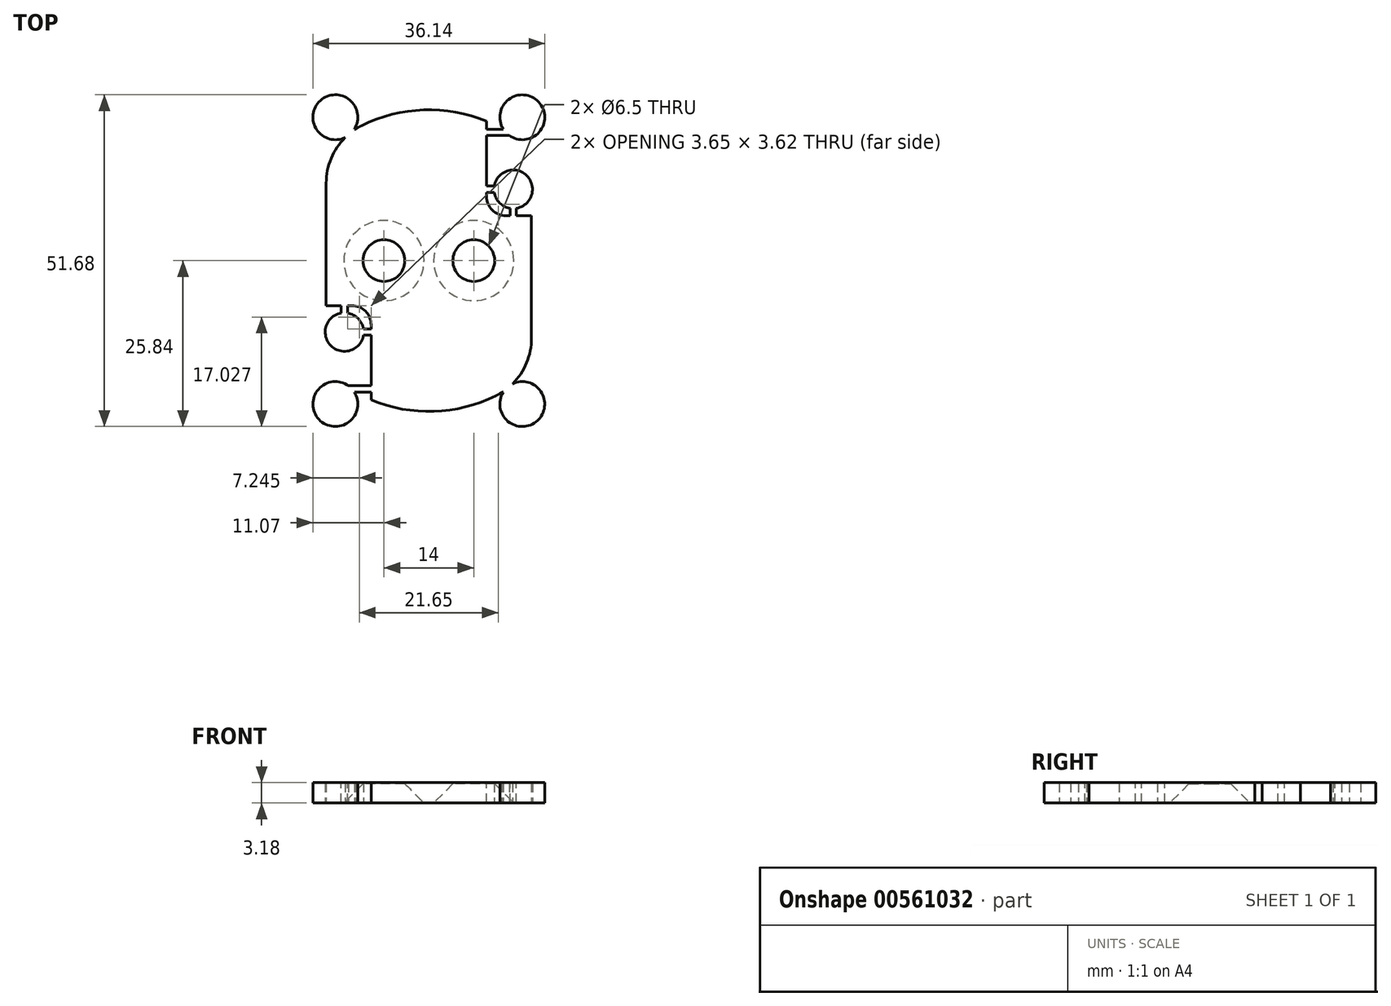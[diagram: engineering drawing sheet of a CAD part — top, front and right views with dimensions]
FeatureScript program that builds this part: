
annotation { "Feature Type Name" : "Feature", "Feature Type Description" : "" }
export const myFeature = defineFeature(function(context is Context, id is Id, definition is map)
    precondition{}
    {
        {
            var Q0;
            Q0=qCreatedBy(makeId("Top.planeOp"),FACE);
            var sketch = newSketch(context, id + "F0", { "sketchPlane" : qUnion([Q0])});
            skArc(sketch, "E0", {"start": v(9, 21.7) * mm, "mid": v(-0.8, 23.49) * mm, "end": v(-10.44, 21.05) * mm});
            skLineSegment(sketch, "E1", {"start": v(9, 21.7) * mm, "end": v(9, 10) * mm});
            skLineSegment(sketch, "E2", {"start": v(12, 7) * mm, "end": v(16, 7) * mm});
            skLineSegment(sketch, "E3", {"start": v(-9, -21.7) * mm, "end": v(-9, -10) * mm});
            skLineSegment(sketch, "E4", {"start": v(-12, -7) * mm, "end": v(-16, -7) * mm});
            skArc(sketch, "E5.trimOffspring", {"start": v(-9, -21.7) * mm, "mid": v(0.8, -23.49) * mm, "end": v(10.44, -21.05) * mm});
            skLineSegment(sketch, "E6", {"start": v(-16, -7) * mm, "end": v(-16, 12.1) * mm});
            skLineSegment(sketch, "E7", {"start": v(16, 7) * mm, "end": v(16, -12.1) * mm});
            skPoint(sketch, "E8.visualSharp", {"position": v(9, 7) * mm});
            skArc(sketch, "E8.filletArc", {"start": v(9, 10) * mm, "mid": v(9.88, 7.88) * mm, "end": v(12, 7) * mm});
            skPoint(sketch, "E9.visualSharp", {"position": v(-9, -7) * mm});
            skArc(sketch, "E9.filletArc", {"start": v(-9, -10) * mm, "mid": v(-9.88, -7.88) * mm, "end": v(-12, -7) * mm});
            skPoint(sketch, "E10.visualSharp", {"position": v(16, -17.21) * mm});
            skArc(sketch, "E10.filletArc", {"start": v(10.44, -21.05) * mm, "mid": v(14.5, -17.36) * mm, "end": v(16, -12.1) * mm});
            skPoint(sketch, "E11.visualSharp", {"position": v(-16, 17.21) * mm});
            skArc(sketch, "E11.filletArc", {"start": v(-10.44, 21.05) * mm, "mid": v(-14.5, 17.36) * mm, "end": v(-16, 12.1) * mm});
            skCircle(sketch, "E12", {"center": v(-25, -13.13) * mm, "radius": 2.75 * mm, "construction": true});
            skCircle(sketch, "E13.0", {"center": v(-25, -13.13) * mm, "radius": 3.75 * mm, "construction": true});
            skLineSegment(sketch, "E14", {"start": v(-16, 0) * mm, "end": v(16, 0) * mm, "construction": true});
            skLineSegment(sketch, "E15", {"start": v(0, 23.5) * mm, "end": v(0, -23.5) * mm, "construction": true});
            skCircle(sketch, "E16", {"center": v(-7, 0) * mm, "radius": 3.25 * mm});
            skCircle(sketch, "E17", {"center": v(7, 0) * mm, "radius": 3.25 * mm});
            skSolve(sketch);
        }
        {
            var Q0;
            Q0 = qSketchRegion(id + "F0", true);
            extrude(context, id + "F1", {"entities" : qUnion([Q0]), "depth" : 3.17 * mm, "offsetDistance" : 25 * mm});
        }
        {
            var Q0;
            Q0=makeQuery(id+"F1.opExtrude","CAP_EDGE",EDGE,{"disambiguationData":[OSD([sQuery(id+"F0.wireOp",EDGE,"E16")])],"isStart":true});
            var Q1;
            Q1=makeQuery(id+"F1.opExtrude","CAP_EDGE",EDGE,{"disambiguationData":[OSD([sQuery(id+"F0.wireOp",EDGE,"E17")])],"isStart":true});
            chamfer(context, id + "F2", {"entities" : qUnion([Q0, Q1]), "width" : 3 * mm, "tangentPropagation" : true});
        }
        {
            var Q0;
            {var subQ0=sQuery(id+"F0.wireOp",EDGE,"E11.filletArc");var subQ1=sQuery(id+"F0.wireOp",EDGE,"E10.filletArc");var subQ2=sQuery(id+"F0.wireOp",EDGE,"E9.filletArc");var subQ3=sQuery(id+"F0.wireOp",EDGE,"E2");var subQ4=sQuery(id+"F0.wireOp",EDGE,"E1");var subQ5=sQuery(id+"F0.wireOp",EDGE,"E17");var subQ6=sQuery(id+"F0.wireOp",EDGE,"E16");var subQ7=sQuery(id+"F0.wireOp",EDGE,"E8.filletArc");var subQ8=sQuery(id+"F0.wireOp",EDGE,"E7");var subQ9=sQuery(id+"F0.wireOp",EDGE,"E6");var subQ10=sQuery(id+"F0.wireOp",EDGE,"E5.trimOffspring");var subQ11=sQuery(id+"F0.wireOp",EDGE,"E4");var subQ12=sQuery(id+"F0.wireOp",EDGE,"E3");var subQ13=sQuery(id+"F0.wireOp",EDGE,"E0");var subQ14=makeQuery(id+"F1.opExtrude","CAP_FACE",FACE,{"disambiguationData":[OSD([subQ13,subQ4,subQ3,subQ12,subQ11,subQ10,subQ9,subQ8,subQ7,subQ2,subQ1,subQ0,subQ6,subQ5])],"isStart":true});Q0=makeQuery(id+"F7rJXuFzd7whJRI_1.boolean.opBoolean","SPLIT",FACE,{"disambiguationData":[TD([makeQuery(id+"F1.opExtrude","SWEPT_FACE",FACE,{"disambiguationData":[OSD([subQ13])]}),subQ14,makeQuery(id+"F1.opExtrude","SWEPT_FACE",FACE,{"disambiguationData":[OSD([subQ4])]}),makeQuery(id+"F1.opExtrude","SWEPT_FACE",FACE,{"disambiguationData":[OSD([subQ3])]}),makeQuery(id+"F1.opExtrude","SWEPT_FACE",FACE,{"disambiguationData":[OSD([subQ12])]}),makeQuery(id+"F1.opExtrude","SWEPT_FACE",FACE,{"disambiguationData":[OSD([subQ11])]}),makeQuery(id+"F1.opExtrude","SWEPT_FACE",FACE,{"disambiguationData":[OSD([subQ10])]}),makeQuery(id+"F1.opExtrude","SWEPT_FACE",FACE,{"disambiguationData":[OSD([subQ9])]}),makeQuery(id+"F1.opExtrude","SWEPT_FACE",FACE,{"disambiguationData":[OSD([subQ8])]}),makeQuery(id+"F1.opExtrude","SWEPT_FACE",FACE,{"disambiguationData":[OSD([subQ7])]}),makeQuery(id+"F1.opExtrude","SWEPT_FACE",FACE,{"disambiguationData":[OSD([subQ2])]}),makeQuery(id+"F1.opExtrude","SWEPT_FACE",FACE,{"disambiguationData":[OSD([subQ1])]}),makeQuery(id+"F1.opExtrude","SWEPT_FACE",FACE,{"disambiguationData":[OSD([subQ0])]}),makeQuery(id+"F2.opChamfer","BLEND_FACE",FACE,{"disambiguationData":[OSD([subQ6])]}),makeQuery(id+"F2.opChamfer","BLEND_FACE",FACE,{"disambiguationData":[OSD([subQ5])]}),makeQuery(id+"FJRN7x09wjddpbt_1.opExtrude","SWEPT_FACE",FACE,{"disambiguationData":[OSD([sQuery(id+"F7eSavBRXq2dsKI_1.wireOp",EDGE,"8fa0daad-dcc6-40bc-96bb-e75cae0788b3.0"),sQuery(id+"F7eSavBRXq2dsKI_1.wireOp",EDGE,"n97fCblB-dYT1-Ae0N-i9l5-hArpFE4WxoEw"),sQuery(id+"F7eSavBRXq2dsKI_1.wireOp",EDGE,"zqmUF0HG-ZMKi-8qrd-Ef0Q-vBSs0Mmfe9LQ")])]}),makeQuery(id+"FJRN7x09wjddpbt_1.opExtrude","SWEPT_FACE",FACE,{"disambiguationData":[OSD([sQuery(id+"F7eSavBRXq2dsKI_1.wireOp",EDGE,"e7dde7e7-45df-4180-b28b-b804ea4044e9.0"),sQuery(id+"F7eSavBRXq2dsKI_1.wireOp",EDGE,"sIQKzWda-6bcH-76ju-v0o7-Y5VWPazvYRRh")])]}),makeQuery(id+"FJRN7x09wjddpbt_1.opExtrude","SWEPT_FACE",FACE,{"disambiguationData":[OSD([sQuery(id+"F7eSavBRXq2dsKI_1.wireOp",EDGE,"e2ec28e7-3c61-4beb-a361-8ff4288dedb5.0"),sQuery(id+"F7eSavBRXq2dsKI_1.wireOp",EDGE,"FANFZC1z-x6Kr-yiFN-UvMI-yiw826xu6Ap1"),sQuery(id+"F7eSavBRXq2dsKI_1.wireOp",EDGE,"g5gt4XFT-gkoA-6hYA-Hcyk-9ZKPAERTy8uj")])]}),makeQuery(id+"FJRN7x09wjddpbt_1.opExtrude","SWEPT_FACE",FACE,{"disambiguationData":[OSD([sQuery(id+"F7eSavBRXq2dsKI_1.wireOp",EDGE,"114f5c74-5dc2-4418-9fc7-5e99572f52d0.0"),sQuery(id+"F7eSavBRXq2dsKI_1.wireOp",EDGE,"zSLGWUzL-SdZn-Svw3-gUv4-kZl9FifSsFUy")])]}),makeQuery(id+"FJRN7x09wjddpbt_1.opExtrude","SWEPT_FACE",FACE,{"disambiguationData":[OSD([sQuery(id+"F7eSavBRXq2dsKI_1.wireOp",EDGE,"nJadRcHw-teo3-5osU-S39U-DkAnWl3BXwkZ")])]}),makeQuery(id+"FJRN7x09wjddpbt_1.opExtrude","SWEPT_FACE",FACE,{"disambiguationData":[OSD([sQuery(id+"F7eSavBRXq2dsKI_1.wireOp",EDGE,"ttBzBW3A-ctuH-0JyX-jzIS-FURpFCNeuO8h")])]}),makeQuery(id+"F7rJXuFzd7whJRI_1.opExtrude","SWEPT_FACE",FACE,{"disambiguationData":[OSD([sQuery(id+"FJmdBiUrNK7vk2C_1.wireOp",EDGE,"6ccd15b6-2c7d-49c7-b1f2-da74a62637db.0")])]}),makeQuery(id+"F7rJXuFzd7whJRI_1.opExtrude","SWEPT_FACE",FACE,{"disambiguationData":[OSD([sQuery(id+"FJmdBiUrNK7vk2C_1.wireOp",EDGE,"40ce07cb-99c2-479f-b22f-8af0174601d0.0")])]}),makeQuery(id+"F7rJXuFzd7whJRI_1.opExtrude","SWEPT_FACE",FACE,{"disambiguationData":[OSD([sQuery(id+"FJmdBiUrNK7vk2C_1.wireOp",EDGE,"78c2ad54-c2ae-4de3-8f60-8a07646ae407.0")])]}),makeQuery(id+"F7rJXuFzd7whJRI_1.opExtrude","SWEPT_FACE",FACE,{"disambiguationData":[OSD([sQuery(id+"FJmdBiUrNK7vk2C_1.wireOp",EDGE,"a5992d94-6c83-43fa-9fcd-ea2cdb8489dd.0")])]}),makeQuery(id+"F7rJXuFzd7whJRI_1.opExtrude","SWEPT_FACE",FACE,{"disambiguationData":[OSD([sQuery(id+"FJmdBiUrNK7vk2C_1.wireOp",EDGE,"94c68105-d2c2-4680-80d6-486de9ed9849.0")])]}),makeQuery(id+"F7rJXuFzd7whJRI_1.opExtrude","SWEPT_FACE",FACE,{"disambiguationData":[OSD([sQuery(id+"FJmdBiUrNK7vk2C_1.wireOp",EDGE,"5a1a2a42-ccab-4370-b0ba-2aafa13ec267.0")])]}),makeQuery(id+"F7rJXuFzd7whJRI_1.opExtrude","SWEPT_FACE",FACE,{"disambiguationData":[OSD([sQuery(id+"FJmdBiUrNK7vk2C_1.wireOp",EDGE,"b4e74ed3-bff9-4cb2-9b7f-92468b897526.0")])]}),makeQuery(id+"F7rJXuFzd7whJRI_1.opExtrude","SWEPT_FACE",FACE,{"disambiguationData":[OSD([sQuery(id+"FJmdBiUrNK7vk2C_1.wireOp",EDGE,"bb4724f0-601e-4360-ab2a-57e4bcc06b99.0")])]}),makeQuery(id+"F7rJXuFzd7whJRI_1.opExtrude","SWEPT_FACE",FACE,{"disambiguationData":[OSD([sQuery(id+"FJmdBiUrNK7vk2C_1.wireOp",EDGE,"uudjV1i5-Grv9-P5jP-yEU4-0d5r7IUhJ2e0")])]}),makeQuery(id+"F7rJXuFzd7whJRI_1.opExtrude","SWEPT_FACE",FACE,{"disambiguationData":[OSD([sQuery(id+"FJmdBiUrNK7vk2C_1.wireOp",EDGE,"BnZCvLlh-3Oxl-QPef-bhhu-gMUTPy8vweJf")])]}),makeQuery(id+"F7rJXuFzd7whJRI_1.opExtrude","SWEPT_FACE",FACE,{"disambiguationData":[OSD([sQuery(id+"FJmdBiUrNK7vk2C_1.wireOp",EDGE,"tRLUp6J2-3hZ5-DYTa-A9Ly-egRAl724t58r")])]}),makeQuery(id+"F7rJXuFzd7whJRI_1.opExtrude","SWEPT_FACE",FACE,{"disambiguationData":[OSD([sQuery(id+"FJmdBiUrNK7vk2C_1.wireOp",EDGE,"19JWv38y-xvaW-ymGE-MEyl-ytO9JCIOFrmj")])]})])],"derivedFrom":subQ14});}
            var sketch = newSketch(context, id + "F3", { "sketchPlane" : qUnion([Q0])});
            skCircle(sketch, "E18", {"center": v(-13.15, 11.12) * mm, "radius": 3 * mm});
            skLineSegment(sketch, "E19", {"start": v(-7, 0) * mm, "end": v(7, 0) * mm, "construction": true});
            skLineSegment(sketch, "E20", {"start": v(0, 7) * mm, "end": v(0, -7) * mm, "construction": true});
            skCircle(sketch, "E21.MirrorC", {"center": v(13.15, -11.12) * mm, "radius": 3 * mm});
            skLineSegment(sketch, "E22.bottom", {"start": v(-6, 11.62) * mm, "end": v(-12, 11.62) * mm});
            skLineSegment(sketch, "E22.top", {"start": v(-6, 10.62) * mm, "end": v(-12, 10.62) * mm});
            skLineSegment(sketch, "E22.left", {"start": v(-6, 11.62) * mm, "end": v(-6, 10.62) * mm});
            skLineSegment(sketch, "E22.right", {"start": v(-12, 11.62) * mm, "end": v(-12, 10.62) * mm});
            skPoint(sketch, "E22.middle", {"position": v(-9, 11.12) * mm});
            skLineSegment(sketch, "E23.bottom", {"start": v(-12.65, 4) * mm, "end": v(-13.65, 4) * mm});
            skLineSegment(sketch, "E23.top", {"start": v(-12.65, 10) * mm, "end": v(-13.65, 10) * mm});
            skLineSegment(sketch, "E23.left", {"start": v(-12.65, 4) * mm, "end": v(-12.65, 10) * mm});
            skLineSegment(sketch, "E23.right", {"start": v(-13.65, 4) * mm, "end": v(-13.65, 10) * mm});
            skPoint(sketch, "E23.middle", {"position": v(-13.15, 7) * mm});
            skLineSegment(sketch, "E24.bottom", {"start": v(13.65, -4) * mm, "end": v(12.65, -4) * mm});
            skLineSegment(sketch, "E24.top", {"start": v(13.65, -10) * mm, "end": v(12.65, -10) * mm});
            skLineSegment(sketch, "E24.left", {"start": v(13.65, -4) * mm, "end": v(13.65, -10) * mm});
            skLineSegment(sketch, "E24.right", {"start": v(12.65, -4) * mm, "end": v(12.65, -10) * mm});
            skPoint(sketch, "E24.middle", {"position": v(13.15, -7) * mm});
            skLineSegment(sketch, "E25.bottom", {"start": v(6, -11.62) * mm, "end": v(12, -11.62) * mm});
            skLineSegment(sketch, "E25.top", {"start": v(6, -10.62) * mm, "end": v(12, -10.62) * mm});
            skLineSegment(sketch, "E25.left", {"start": v(6, -11.62) * mm, "end": v(6, -10.62) * mm});
            skLineSegment(sketch, "E25.right", {"start": v(12, -11.62) * mm, "end": v(12, -10.62) * mm});
            skPoint(sketch, "E25.middle", {"position": v(9, -11.12) * mm});
            skSolve(sketch);
        }
        {
            var Q0;
            Q0 = qSketchRegion(id + "F3", true);
            var Q1;
            Q1=makeQuery(id+"F1.opExtrude","CAP_FACE",FACE,{"disambiguationData":[OSD([sQuery(id+"F0.wireOp",EDGE,"E0"),sQuery(id+"F0.wireOp",EDGE,"E1"),sQuery(id+"F0.wireOp",EDGE,"E2"),sQuery(id+"F0.wireOp",EDGE,"E3"),sQuery(id+"F0.wireOp",EDGE,"E4"),sQuery(id+"F0.wireOp",EDGE,"E5.trimOffspring"),sQuery(id+"F0.wireOp",EDGE,"E6"),sQuery(id+"F0.wireOp",EDGE,"E7"),sQuery(id+"F0.wireOp",EDGE,"E8.filletArc"),sQuery(id+"F0.wireOp",EDGE,"E9.filletArc"),sQuery(id+"F0.wireOp",EDGE,"E10.filletArc"),sQuery(id+"F0.wireOp",EDGE,"E11.filletArc"),sQuery(id+"F0.wireOp",EDGE,"E16"),sQuery(id+"F0.wireOp",EDGE,"E17")])],"isStart":false});
            extrude(context, id + "F4", {"entities" : qUnion([Q0]), "operationType" : NewBodyOperationType.ADD, "endBound" : BoundingType.UP_TO_SURFACE, "oppositeDirection" : true, "depth" : 25 * mm, "endBoundEntityFace" : qUnion([Q1]), "offsetDistance" : 25 * mm});
        }
        {
            var Q0;
            {var subQ0=sQuery(id+"F0.wireOp",EDGE,"E11.filletArc");var subQ1=sQuery(id+"F0.wireOp",EDGE,"E10.filletArc");var subQ2=sQuery(id+"F0.wireOp",EDGE,"E9.filletArc");var subQ3=sQuery(id+"F0.wireOp",EDGE,"E2");var subQ4=sQuery(id+"F0.wireOp",EDGE,"E1");var subQ5=sQuery(id+"F0.wireOp",EDGE,"E17");var subQ6=sQuery(id+"F0.wireOp",EDGE,"E16");var subQ7=sQuery(id+"F0.wireOp",EDGE,"E8.filletArc");var subQ8=sQuery(id+"F0.wireOp",EDGE,"E7");var subQ9=sQuery(id+"F0.wireOp",EDGE,"E6");var subQ10=sQuery(id+"F0.wireOp",EDGE,"E5.trimOffspring");var subQ11=sQuery(id+"F0.wireOp",EDGE,"E4");var subQ12=sQuery(id+"F0.wireOp",EDGE,"E3");var subQ13=sQuery(id+"F0.wireOp",EDGE,"E0");var subQ14=makeQuery(id+"F1.opExtrude","CAP_FACE",FACE,{"disambiguationData":[OSD([subQ13,subQ4,subQ3,subQ12,subQ11,subQ10,subQ9,subQ8,subQ7,subQ2,subQ1,subQ0,subQ6,subQ5])],"isStart":true});Q0=makeQuery(id+"F4.boolean.opBoolean","MERGE",FACE,{"derivedFrom":[makeQuery(id+"F7rJXuFzd7whJRI_1.boolean.opBoolean","SPLIT",FACE,{"disambiguationData":[TD([makeQuery(id+"F1.opExtrude","SWEPT_FACE",FACE,{"disambiguationData":[OSD([subQ13])]}),subQ14,makeQuery(id+"F1.opExtrude","SWEPT_FACE",FACE,{"disambiguationData":[OSD([subQ4])]}),makeQuery(id+"F1.opExtrude","SWEPT_FACE",FACE,{"disambiguationData":[OSD([subQ3])]}),makeQuery(id+"F1.opExtrude","SWEPT_FACE",FACE,{"disambiguationData":[OSD([subQ12])]}),makeQuery(id+"F1.opExtrude","SWEPT_FACE",FACE,{"disambiguationData":[OSD([subQ11])]}),makeQuery(id+"F1.opExtrude","SWEPT_FACE",FACE,{"disambiguationData":[OSD([subQ10])]}),makeQuery(id+"F1.opExtrude","SWEPT_FACE",FACE,{"disambiguationData":[OSD([subQ9])]}),makeQuery(id+"F1.opExtrude","SWEPT_FACE",FACE,{"disambiguationData":[OSD([subQ8])]}),makeQuery(id+"F1.opExtrude","SWEPT_FACE",FACE,{"disambiguationData":[OSD([subQ7])]}),makeQuery(id+"F1.opExtrude","SWEPT_FACE",FACE,{"disambiguationData":[OSD([subQ2])]}),makeQuery(id+"F1.opExtrude","SWEPT_FACE",FACE,{"disambiguationData":[OSD([subQ1])]}),makeQuery(id+"F1.opExtrude","SWEPT_FACE",FACE,{"disambiguationData":[OSD([subQ0])]}),makeQuery(id+"F2.opChamfer","BLEND_FACE",FACE,{"disambiguationData":[OSD([subQ6])]}),makeQuery(id+"F2.opChamfer","BLEND_FACE",FACE,{"disambiguationData":[OSD([subQ5])]}),makeQuery(id+"FJRN7x09wjddpbt_1.opExtrude","SWEPT_FACE",FACE,{"disambiguationData":[OSD([sQuery(id+"F7eSavBRXq2dsKI_1.wireOp",EDGE,"8fa0daad-dcc6-40bc-96bb-e75cae0788b3.0"),sQuery(id+"F7eSavBRXq2dsKI_1.wireOp",EDGE,"n97fCblB-dYT1-Ae0N-i9l5-hArpFE4WxoEw"),sQuery(id+"F7eSavBRXq2dsKI_1.wireOp",EDGE,"zqmUF0HG-ZMKi-8qrd-Ef0Q-vBSs0Mmfe9LQ")])]}),makeQuery(id+"FJRN7x09wjddpbt_1.opExtrude","SWEPT_FACE",FACE,{"disambiguationData":[OSD([sQuery(id+"F7eSavBRXq2dsKI_1.wireOp",EDGE,"e7dde7e7-45df-4180-b28b-b804ea4044e9.0"),sQuery(id+"F7eSavBRXq2dsKI_1.wireOp",EDGE,"sIQKzWda-6bcH-76ju-v0o7-Y5VWPazvYRRh")])]}),makeQuery(id+"FJRN7x09wjddpbt_1.opExtrude","SWEPT_FACE",FACE,{"disambiguationData":[OSD([sQuery(id+"F7eSavBRXq2dsKI_1.wireOp",EDGE,"e2ec28e7-3c61-4beb-a361-8ff4288dedb5.0"),sQuery(id+"F7eSavBRXq2dsKI_1.wireOp",EDGE,"FANFZC1z-x6Kr-yiFN-UvMI-yiw826xu6Ap1"),sQuery(id+"F7eSavBRXq2dsKI_1.wireOp",EDGE,"g5gt4XFT-gkoA-6hYA-Hcyk-9ZKPAERTy8uj")])]}),makeQuery(id+"FJRN7x09wjddpbt_1.opExtrude","SWEPT_FACE",FACE,{"disambiguationData":[OSD([sQuery(id+"F7eSavBRXq2dsKI_1.wireOp",EDGE,"114f5c74-5dc2-4418-9fc7-5e99572f52d0.0"),sQuery(id+"F7eSavBRXq2dsKI_1.wireOp",EDGE,"zSLGWUzL-SdZn-Svw3-gUv4-kZl9FifSsFUy")])]}),makeQuery(id+"FJRN7x09wjddpbt_1.opExtrude","SWEPT_FACE",FACE,{"disambiguationData":[OSD([sQuery(id+"F7eSavBRXq2dsKI_1.wireOp",EDGE,"nJadRcHw-teo3-5osU-S39U-DkAnWl3BXwkZ")])]}),makeQuery(id+"FJRN7x09wjddpbt_1.opExtrude","SWEPT_FACE",FACE,{"disambiguationData":[OSD([sQuery(id+"F7eSavBRXq2dsKI_1.wireOp",EDGE,"ttBzBW3A-ctuH-0JyX-jzIS-FURpFCNeuO8h")])]}),makeQuery(id+"F7rJXuFzd7whJRI_1.opExtrude","SWEPT_FACE",FACE,{"disambiguationData":[OSD([sQuery(id+"FJmdBiUrNK7vk2C_1.wireOp",EDGE,"6ccd15b6-2c7d-49c7-b1f2-da74a62637db.0")])]}),makeQuery(id+"F7rJXuFzd7whJRI_1.opExtrude","SWEPT_FACE",FACE,{"disambiguationData":[OSD([sQuery(id+"FJmdBiUrNK7vk2C_1.wireOp",EDGE,"40ce07cb-99c2-479f-b22f-8af0174601d0.0")])]}),makeQuery(id+"F7rJXuFzd7whJRI_1.opExtrude","SWEPT_FACE",FACE,{"disambiguationData":[OSD([sQuery(id+"FJmdBiUrNK7vk2C_1.wireOp",EDGE,"78c2ad54-c2ae-4de3-8f60-8a07646ae407.0")])]}),makeQuery(id+"F7rJXuFzd7whJRI_1.opExtrude","SWEPT_FACE",FACE,{"disambiguationData":[OSD([sQuery(id+"FJmdBiUrNK7vk2C_1.wireOp",EDGE,"a5992d94-6c83-43fa-9fcd-ea2cdb8489dd.0")])]}),makeQuery(id+"F7rJXuFzd7whJRI_1.opExtrude","SWEPT_FACE",FACE,{"disambiguationData":[OSD([sQuery(id+"FJmdBiUrNK7vk2C_1.wireOp",EDGE,"94c68105-d2c2-4680-80d6-486de9ed9849.0")])]}),makeQuery(id+"F7rJXuFzd7whJRI_1.opExtrude","SWEPT_FACE",FACE,{"disambiguationData":[OSD([sQuery(id+"FJmdBiUrNK7vk2C_1.wireOp",EDGE,"5a1a2a42-ccab-4370-b0ba-2aafa13ec267.0")])]}),makeQuery(id+"F7rJXuFzd7whJRI_1.opExtrude","SWEPT_FACE",FACE,{"disambiguationData":[OSD([sQuery(id+"FJmdBiUrNK7vk2C_1.wireOp",EDGE,"b4e74ed3-bff9-4cb2-9b7f-92468b897526.0")])]}),makeQuery(id+"F7rJXuFzd7whJRI_1.opExtrude","SWEPT_FACE",FACE,{"disambiguationData":[OSD([sQuery(id+"FJmdBiUrNK7vk2C_1.wireOp",EDGE,"bb4724f0-601e-4360-ab2a-57e4bcc06b99.0")])]}),makeQuery(id+"F7rJXuFzd7whJRI_1.opExtrude","SWEPT_FACE",FACE,{"disambiguationData":[OSD([sQuery(id+"FJmdBiUrNK7vk2C_1.wireOp",EDGE,"uudjV1i5-Grv9-P5jP-yEU4-0d5r7IUhJ2e0")])]}),makeQuery(id+"F7rJXuFzd7whJRI_1.opExtrude","SWEPT_FACE",FACE,{"disambiguationData":[OSD([sQuery(id+"FJmdBiUrNK7vk2C_1.wireOp",EDGE,"BnZCvLlh-3Oxl-QPef-bhhu-gMUTPy8vweJf")])]}),makeQuery(id+"F7rJXuFzd7whJRI_1.opExtrude","SWEPT_FACE",FACE,{"disambiguationData":[OSD([sQuery(id+"FJmdBiUrNK7vk2C_1.wireOp",EDGE,"tRLUp6J2-3hZ5-DYTa-A9Ly-egRAl724t58r")])]}),makeQuery(id+"F7rJXuFzd7whJRI_1.opExtrude","SWEPT_FACE",FACE,{"disambiguationData":[OSD([sQuery(id+"FJmdBiUrNK7vk2C_1.wireOp",EDGE,"19JWv38y-xvaW-ymGE-MEyl-ytO9JCIOFrmj")])]})])],"derivedFrom":subQ14}),makeQuery(id+"F4.opExtrude","CAP_FACE",FACE,{"disambiguationData":[OSD([sQuery(id+"F3.wireOp",EDGE,"E18"),sQuery(id+"F3.wireOp",EDGE,"E22.bottom"),sQuery(id+"F3.wireOp",EDGE,"E22.top"),sQuery(id+"F3.wireOp",EDGE,"E22.left"),sQuery(id+"F3.wireOp",EDGE,"E23.bottom"),sQuery(id+"F3.wireOp",EDGE,"E23.left"),sQuery(id+"F3.wireOp",EDGE,"E23.right")])],"isStart":true}),makeQuery(id+"F4.opExtrude","CAP_FACE",FACE,{"disambiguationData":[OSD([sQuery(id+"F3.wireOp",EDGE,"E21.MirrorC"),sQuery(id+"F3.wireOp",EDGE,"E24.bottom"),sQuery(id+"F3.wireOp",EDGE,"E24.left"),sQuery(id+"F3.wireOp",EDGE,"E24.right"),sQuery(id+"F3.wireOp",EDGE,"E25.bottom"),sQuery(id+"F3.wireOp",EDGE,"E25.top"),sQuery(id+"F3.wireOp",EDGE,"E25.left")])],"isStart":true})]});}
            var sketch = newSketch(context, id + "F5", { "sketchPlane" : qUnion([Q0])});
            skArc(sketch, "E26.0", {"start": v(-18.07, 6.63) * mm, "mid": v(-16.8, 13.23) * mm, "end": v(-13.15, 18.88) * mm, "construction": true});
            skArc(sketch, "E27.0", {"start": v(-13.15, 18.88) * mm, "mid": v(-10.25, 21.17) * mm, "end": v(-6.87, 22.67) * mm, "construction": true});
            skArc(sketch, "E28.0", {"start": v(-6.87, 22.67) * mm, "mid": v(0, 23.69) * mm, "end": v(6.87, 22.67) * mm, "construction": true});
            skArc(sketch, "E29.0", {"start": v(6.87, 22.67) * mm, "mid": v(10.21, 21.17) * mm, "end": v(13.07, 18.9) * mm, "construction": true});
            skArc(sketch, "E30.0", {"start": v(13.07, 18.9) * mm, "mid": v(16.77, 13.25) * mm, "end": v(18.07, 6.63) * mm, "construction": true});
            skLineSegment(sketch, "E31.0", {"start": v(18.07, 6.63) * mm, "end": v(18.07, -6.62) * mm, "construction": true});
            skArc(sketch, "E32.0", {"start": v(18.07, -6.62) * mm, "mid": v(16.77, -13.25) * mm, "end": v(13.07, -18.9) * mm, "construction": true});
            skArc(sketch, "E33.0", {"start": v(13.07, -18.9) * mm, "mid": v(10.21, -21.17) * mm, "end": v(6.87, -22.67) * mm, "construction": true});
            skArc(sketch, "E34.0", {"start": v(6.87, -22.67) * mm, "mid": v(0, -23.69) * mm, "end": v(-6.87, -22.67) * mm, "construction": true});
            skArc(sketch, "E35.0", {"start": v(-6.87, -22.67) * mm, "mid": v(-10.21, -21.17) * mm, "end": v(-13.07, -18.9) * mm, "construction": true});
            skArc(sketch, "E36.0", {"start": v(-13.07, -18.9) * mm, "mid": v(-16.77, -13.25) * mm, "end": v(-18.07, -6.62) * mm, "construction": true});
            skLineSegment(sketch, "E37.0", {"start": v(-18.07, -6.62) * mm, "end": v(-18.07, -0.5) * mm, "construction": true});
            skLineSegment(sketch, "E38.0", {"start": v(-18.07, 1.98) * mm, "end": v(-18.07, 6.63) * mm, "construction": true});
            skCircle(sketch, "E39", {"center": v(-14.57, 22.34) * mm, "radius": 3.5 * mm});
            skLineSegment(sketch, "E40", {"start": v(-7, 0) * mm, "end": v(7, 0) * mm, "construction": true});
            skLineSegment(sketch, "E41", {"start": v(0, 8.72) * mm, "end": v(0, -8.72) * mm, "construction": true});
            skCircle(sketch, "E42.MirrorC", {"center": v(-14.57, -22.34) * mm, "radius": 3.5 * mm});
            skCircle(sketch, "E43.MirrorC", {"center": v(14.57, 22.34) * mm, "radius": 3.5 * mm});
            skCircle(sketch, "E44.MirrorC", {"center": v(14.57, -22.34) * mm, "radius": 3.5 * mm});
            skLineSegment(sketch, "E45.bottom", {"start": v(-4.45, 19.5) * mm, "end": v(-13.55, 19.5) * mm});
            skLineSegment(sketch, "E45.top", {"start": v(-4.45, 20.5) * mm, "end": v(-13.55, 20.5) * mm});
            skLineSegment(sketch, "E45.left", {"start": v(-4.45, 19.5) * mm, "end": v(-4.45, 20.5) * mm});
            skLineSegment(sketch, "E45.right", {"start": v(-13.55, 19.5) * mm, "end": v(-13.55, 20.5) * mm});
            skPoint(sketch, "E45.middle", {"position": v(-9, 20) * mm});
            skLineSegment(sketch, "E46.MirrorCS", {"start": v(-4.45, -19.5) * mm, "end": v(-13.55, -19.5) * mm});
            skLineSegment(sketch, "E47.MirrorCS", {"start": v(-13.55, -19.5) * mm, "end": v(-13.55, -20.5) * mm});
            skLineSegment(sketch, "E48.MirrorCS", {"start": v(-4.45, -20.5) * mm, "end": v(-13.55, -20.5) * mm});
            skLineSegment(sketch, "E49.MirrorCS", {"start": v(-4.45, -19.5) * mm, "end": v(-4.45, -20.5) * mm});
            skLineSegment(sketch, "E50.MirrorCS", {"start": v(4.45, 19.5) * mm, "end": v(13.55, 19.5) * mm});
            skLineSegment(sketch, "E51.MirrorCS", {"start": v(13.55, 19.5) * mm, "end": v(13.55, 20.5) * mm});
            skLineSegment(sketch, "E52.MirrorCS", {"start": v(4.45, 20.5) * mm, "end": v(13.55, 20.5) * mm});
            skLineSegment(sketch, "E53.MirrorCS", {"start": v(4.45, 19.5) * mm, "end": v(4.45, 20.5) * mm});
            skLineSegment(sketch, "E54.MirrorCS", {"start": v(4.45, -20.5) * mm, "end": v(13.55, -20.5) * mm});
            skLineSegment(sketch, "E55.MirrorCS", {"start": v(13.55, -19.5) * mm, "end": v(13.55, -20.5) * mm});
            skLineSegment(sketch, "E56.MirrorCS", {"start": v(4.45, -19.5) * mm, "end": v(13.55, -19.5) * mm});
            skLineSegment(sketch, "E57.MirrorCS", {"start": v(4.45, -19.5) * mm, "end": v(4.45, -20.5) * mm});
            skSolve(sketch);
        }
        {
            var Q0;
            Q0 = qSketchRegion(id + "F5", true);
            var Q1;
            {var subQ0=sQuery(id+"F0.wireOp",EDGE,"E17");var subQ1=sQuery(id+"F0.wireOp",EDGE,"E16");var subQ2=sQuery(id+"F0.wireOp",EDGE,"E11.filletArc");var subQ3=sQuery(id+"F0.wireOp",EDGE,"E10.filletArc");var subQ4=sQuery(id+"F0.wireOp",EDGE,"E9.filletArc");var subQ5=sQuery(id+"F0.wireOp",EDGE,"E8.filletArc");var subQ6=sQuery(id+"F0.wireOp",EDGE,"E7");var subQ7=sQuery(id+"F0.wireOp",EDGE,"E6");var subQ8=sQuery(id+"F0.wireOp",EDGE,"E5.trimOffspring");var subQ9=sQuery(id+"F0.wireOp",EDGE,"E4");var subQ10=sQuery(id+"F0.wireOp",EDGE,"E3");var subQ11=sQuery(id+"F0.wireOp",EDGE,"E2");var subQ12=sQuery(id+"F0.wireOp",EDGE,"E1");var subQ13=sQuery(id+"F0.wireOp",EDGE,"E0");Q1=makeQuery(id+"F4.boolean.opBoolean","MERGE",FACE,{"derivedFrom":[makeQuery(id+"F1.opExtrude","CAP_FACE",FACE,{"disambiguationData":[OSD([subQ13,subQ12,subQ11,subQ10,subQ9,subQ8,subQ7,subQ6,subQ5,subQ4,subQ3,subQ2,subQ1,subQ0])],"isStart":false}),makeQuery(id+"F4.opExtrude","CAP_FACE",FACE,{"disambiguationData":[OSD([subQ13,subQ12,subQ11,subQ10,subQ9,subQ8,subQ7,subQ6,subQ5,subQ4,subQ3,subQ2,subQ1,subQ0]),OD(0.0)],"isStart":false}),makeQuery(id+"F4.opExtrude","CAP_FACE",FACE,{"disambiguationData":[OSD([subQ13,subQ12,subQ11,subQ10,subQ9,subQ8,subQ7,subQ6,subQ5,subQ4,subQ3,subQ2,subQ1,subQ0]),OD(1.0)],"isStart":false})]});}
            extrude(context, id + "F6", {"entities" : qUnion([Q0]), "operationType" : NewBodyOperationType.ADD, "endBound" : BoundingType.UP_TO_SURFACE, "oppositeDirection" : true, "depth" : 25 * mm, "endBoundEntityFace" : qUnion([Q1]), "offsetDistance" : 25 * mm});
        }
    });
